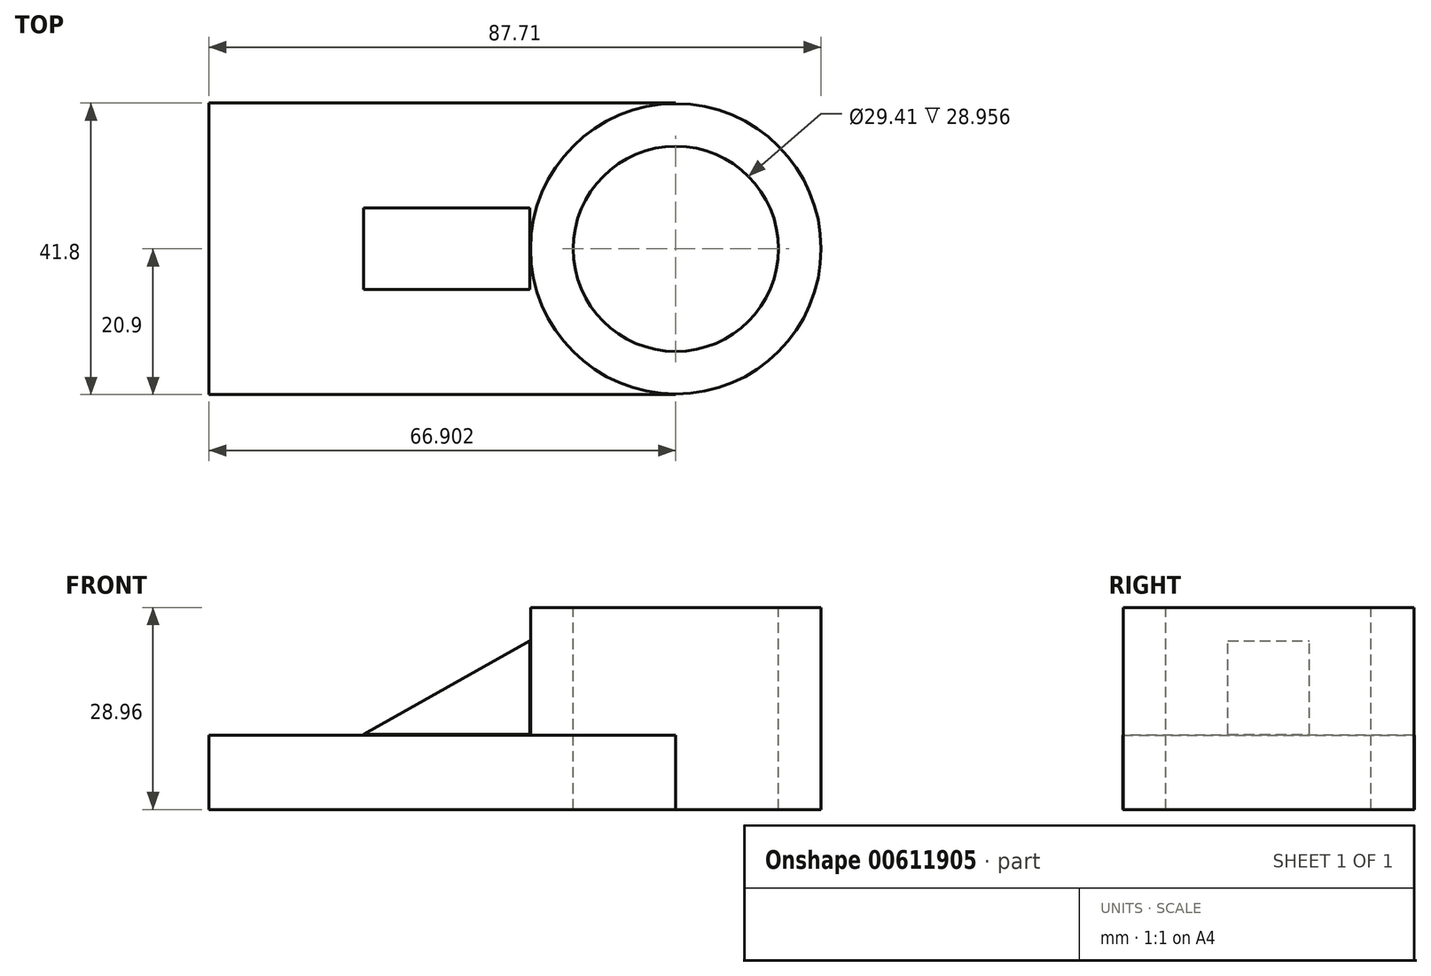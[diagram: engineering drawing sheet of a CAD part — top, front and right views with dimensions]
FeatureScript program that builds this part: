
annotation { "Feature Type Name" : "Feature", "Feature Type Description" : "" }
export const myFeature = defineFeature(function(context is Context, id is Id, definition is map)
    precondition{}
    {
        {
            var Q0;
            Q0=qCreatedBy(makeId("Top.planeOp"),FACE);
            var sketch = newSketch(context, id + "F0", { "sketchPlane" : qUnion([Q0])});
            skLineSegment(sketch, "E0.bottom", {"start": v(33.45, -20.9) * mm, "end": v(-33.45, -20.9) * mm});
            skLineSegment(sketch, "E0.top", {"start": v(33.45, 20.9) * mm, "end": v(-33.45, 20.9) * mm});
            skLineSegment(sketch, "E0.left", {"start": v(33.45, -20.9) * mm, "end": v(33.45, 20.9) * mm});
            skLineSegment(sketch, "E0.right", {"start": v(-33.45, -20.9) * mm, "end": v(-33.45, 20.9) * mm});
            skPoint(sketch, "E0.middle", {"position": v(0, 0) * mm});
            skSolve(sketch);
        }
        {
            var Q0;
            Q0=qCreatedBy(makeId("Top.planeOp"),FACE);
            var sketch = newSketch(context, id + "F1", { "sketchPlane" : qUnion([Q0])});
            skCircle(sketch, "E1", {"center": v(33.45, 0) * mm, "radius": 20.81 * mm});
            skSolve(sketch);
        }
        {
            var Q0;
            Q0=makeQuery(id+"F0.imprint","IMPRINT",FACE,{"disambiguationData":[TD([[makeQuery(id+"F0.imprint","IMPRINT",EDGE,{"derivedFrom":sQuery(id+"F0.wireOp",EDGE,"E0.bottom")}),-1.0]])]});
            extrude(context, id + "F2", {"entities" : qUnion([Q0]), "depth" : 10.67 * mm, "offsetDistance" : 25.4 * mm});
        }
        {
            var Q0;
            Q0=makeQuery(id+"F1.imprint","IMPRINT",FACE,{"disambiguationData":[TD([[makeQuery(id+"F1.imprint","IMPRINT",EDGE,{"derivedFrom":sQuery(id+"F1.wireOp",EDGE,"E1")}),1.0]])]});
            extrude(context, id + "F3", {"entities" : qUnion([Q0]), "operationType" : NewBodyOperationType.ADD, "depth" : 28.96 * mm, "offsetDistance" : 25.4 * mm});
        }
        {
            var Q0;
            Q0=makeQuery(id+"F3.opExtrude","CAP_FACE",FACE,{"disambiguationData":[OSD([sQuery(id+"F1.wireOp",EDGE,"E1")])],"isStart":false});
            var sketch = newSketch(context, id + "F4", { "sketchPlane" : qUnion([Q0])});
            skCircle(sketch, "E2", {"center": v(33.45, 0) * mm, "radius": 14.7 * mm});
            skSolve(sketch);
        }
        {
            var Q0;
            Q0=makeQuery(id+"F4.imprint","IMPRINT",FACE,{"disambiguationData":[TD([[makeQuery(id+"F4.imprint","IMPRINT",EDGE,{"derivedFrom":sQuery(id+"F4.wireOp",EDGE,"E2")}),1.0]])]});
            extrude(context, id + "F5", {"entities" : qUnion([Q0]), "operationType" : NewBodyOperationType.REMOVE, "oppositeDirection" : true, "depth" : 65.02 * mm, "offsetDistance" : 25.4 * mm});
        }
        {
            var Q0;
            Q0=qCreatedBy(makeId("Front.planeOp"),FACE);
            var sketch = newSketch(context, id + "F6", { "sketchPlane" : qUnion([Q0])});
            skLineSegment(sketch, "E3", {"start": v(12.56, 24.2) * mm, "end": v(-11.27, 10.81) * mm});
            skLineSegment(sketch, "E4", {"start": v(-11.27, 10.81) * mm, "end": v(12.56, 10.81) * mm});
            skLineSegment(sketch, "E5", {"start": v(12.56, 10.81) * mm, "end": v(12.56, 24.2) * mm});
            skSolve(sketch);
        }
        {
            var Q0;
            Q0=makeQuery(id+"F6.imprint","IMPRINT",FACE,{"disambiguationData":[TD([[makeQuery(id+"F6.imprint","IMPRINT",EDGE,{"derivedFrom":sQuery(id+"F6.wireOp",EDGE,"E3")}),1.0]])]});
            extrude(context, id + "F7", {"entities" : qUnion([Q0]), "depth" : 5.84 * mm, "offsetDistance" : 25.4 * mm});
        }
        {
            var Q0;
            Q0=makeQuery(id+"F7.opExtrude","CAP_FACE",FACE,{"disambiguationData":[OSD([sQuery(id+"F6.wireOp",EDGE,"E3"),sQuery(id+"F6.wireOp",EDGE,"E4"),sQuery(id+"F6.wireOp",EDGE,"E5")])],"isStart":true});
            extrude(context, id + "F8", {"entities" : qUnion([Q0]), "operationType" : NewBodyOperationType.ADD, "depth" : 5.84 * mm, "offsetDistance" : 25.4 * mm});
        }
    });
